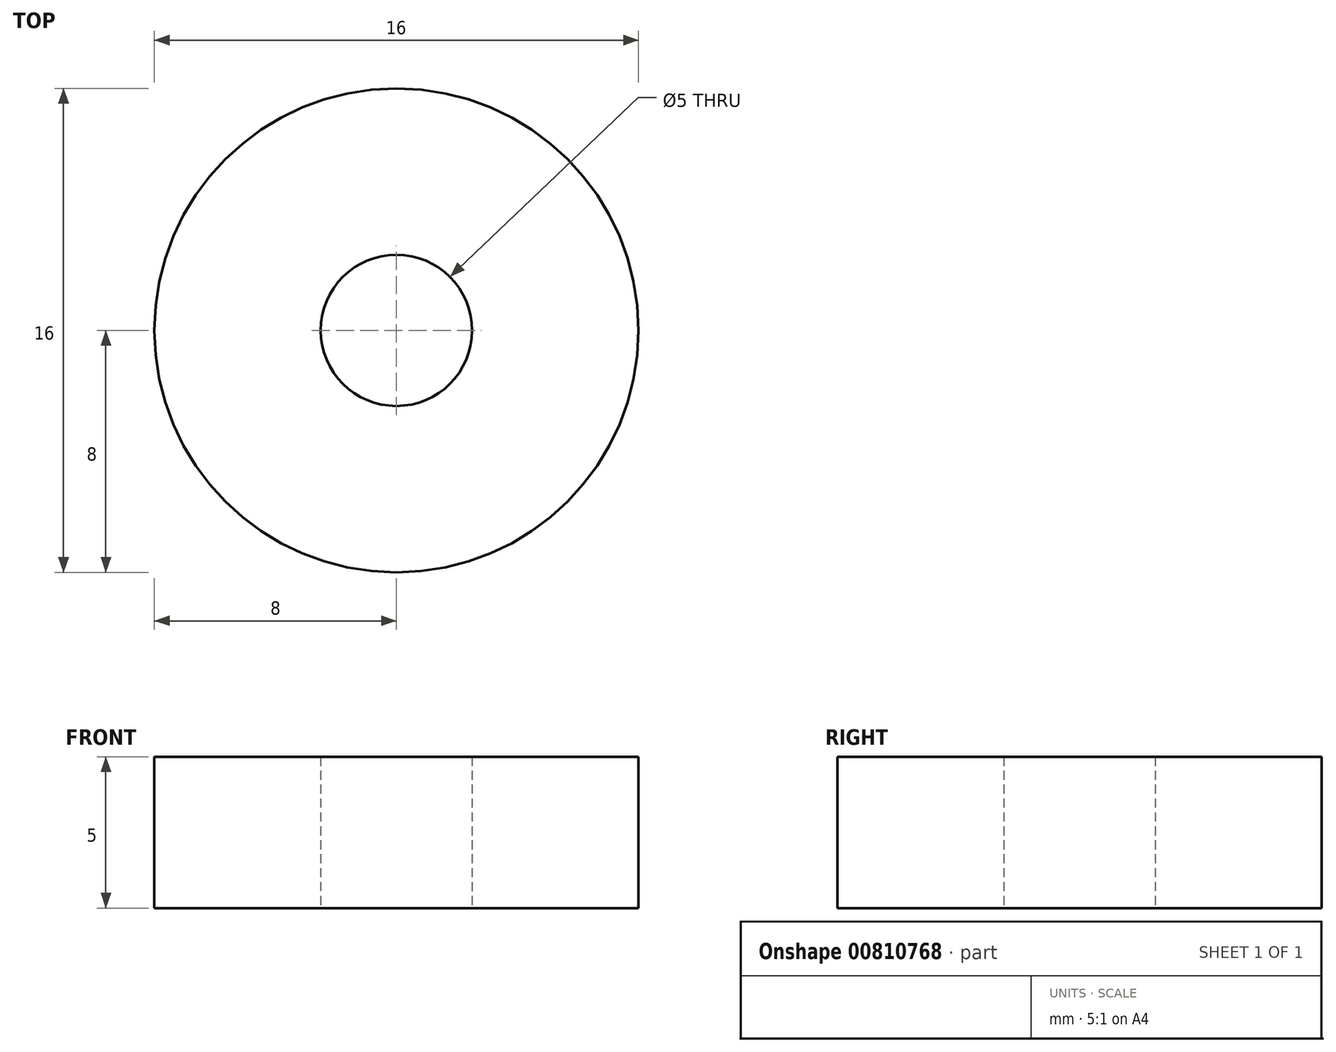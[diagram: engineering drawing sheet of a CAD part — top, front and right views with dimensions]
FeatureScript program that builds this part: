
annotation { "Feature Type Name" : "Feature", "Feature Type Description" : "" }
export const myFeature = defineFeature(function(context is Context, id is Id, definition is map)
    precondition{}
    {
        {
            var Q0;
            Q0=qCreatedBy(makeId("Top.planeOp"),FACE);
            var sketch = newSketch(context, id + "F0", { "sketchPlane" : qUnion([Q0])});
            skCircle(sketch, "E0", {"center": v(0, 0) * mm, "radius": 8 * mm});
            skCircle(sketch, "E1", {"center": v(0, 0) * mm, "radius": 2.5 * mm});
            skSolve(sketch);
        }
        {
            var Q0;
            Q0=qSketchRegion(id+"F0",true);
            extrude(context, id + "F1", {"entities" : qUnion([Q0]), "depth" : 5 * mm, "symmetric" : true});
        }
    });
